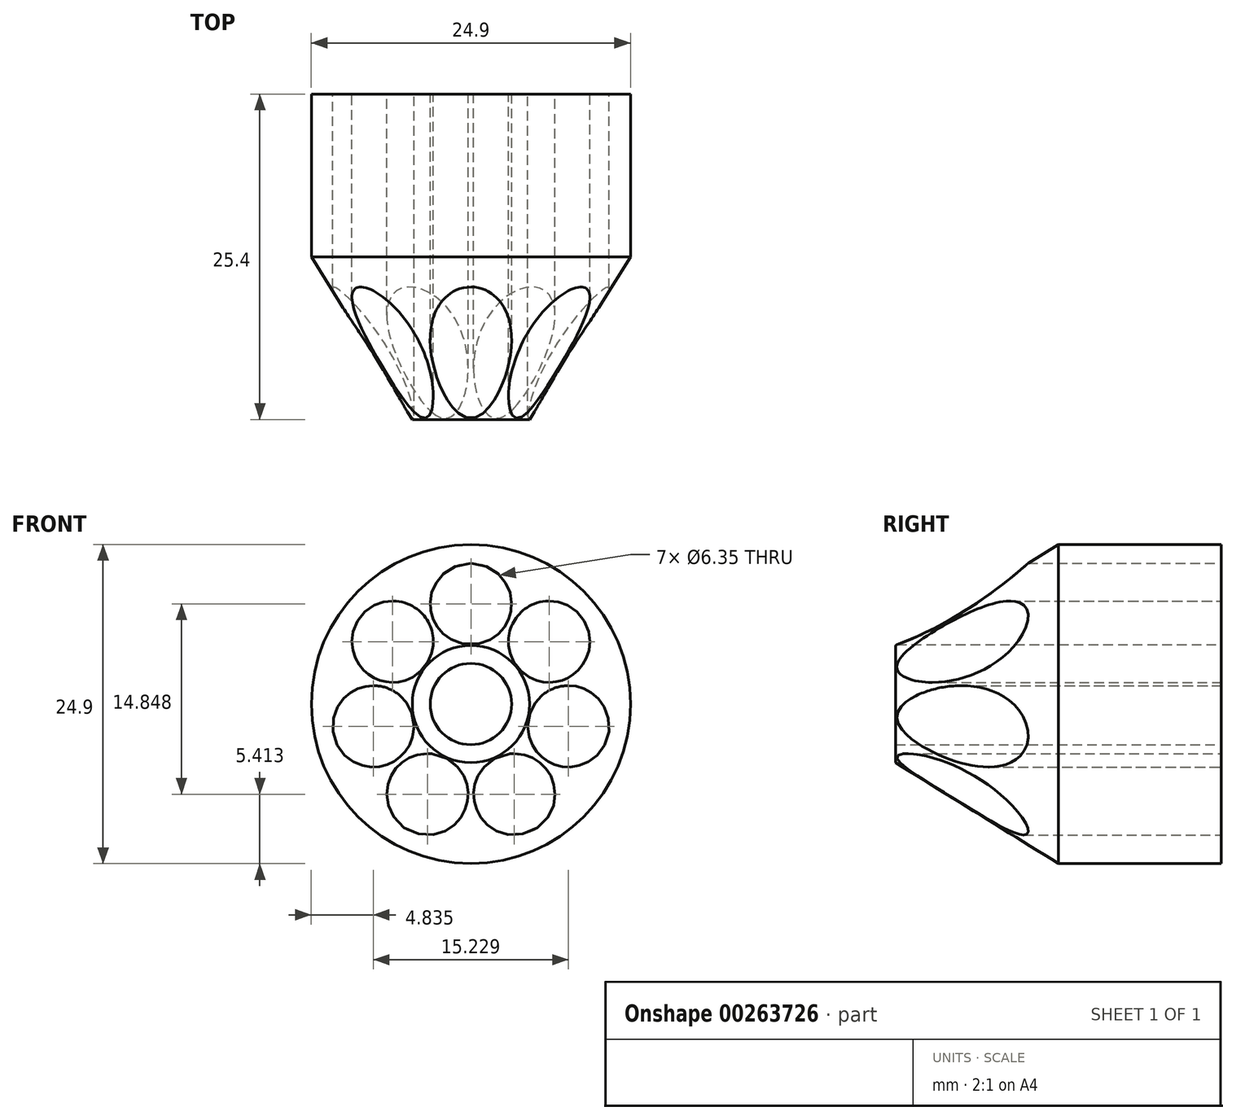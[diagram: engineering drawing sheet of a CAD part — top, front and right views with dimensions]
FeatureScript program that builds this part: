
annotation { "Feature Type Name" : "Feature", "Feature Type Description" : "" }
export const myFeature = defineFeature(function(context is Context, id is Id, definition is map)
    precondition{}
    {
        {
            var Q0;
            Q0=qCreatedBy(makeId("Front.planeOp"),FACE);
            var sketch = newSketch(context, id + "F0", { "sketchPlane" : qUnion([Q0])});
            skCircle(sketch, "E0", {"center": v(0, 0) * mm, "radius": 12.45 * mm});
            skCircle(sketch, "E1", {"center": v(0, 0) * mm, "radius": 3.18 * mm});
            skSolve(sketch);
        }
        {
            var Q0;
            Q0=makeQuery(id+"F0.imprint","IMPRINT",FACE,{"disambiguationData":[TD([[makeQuery(id+"F0.imprint","IMPRINT",EDGE,{"derivedFrom":sQuery(id+"F0.wireOp",EDGE,"E0")}),1.0]])]});
            extrude(context, id + "F1", {"entities" : qUnion([Q0]), "depth" : 25.4 * mm});
        }
        {
            var Q0;
            Q0=makeQuery(id+"F1.opExtrude","CAP_FACE",FACE,{"disambiguationData":[OSD([sQuery(id+"F0.wireOp",EDGE,"E0"),sQuery(id+"F0.wireOp",EDGE,"E1")])],"isStart":true});
            var sketch = newSketch(context, id + "F2", { "sketchPlane" : qUnion([Q0])});
            skLineSegment(sketch, "E2", {"start": v(0, 3.17) * mm, "end": v(0, 12.45) * mm});
            skCircle(sketch, "E3.cCircle", {"center": v(0, 0) * mm, "radius": 7.81 * mm, "construction": true});
            skLineSegment(sketch, "E3.0", {"start": v(0, 7.81) * mm, "end": v(6.1, 4.87) * mm});
            skLineSegment(sketch, "E3.1", {"start": v(6.1, 4.87) * mm, "end": v(7.61, -1.74) * mm});
            skLineSegment(sketch, "E3.2", {"start": v(7.61, -1.74) * mm, "end": v(3.39, -7.04) * mm});
            skLineSegment(sketch, "E3.3", {"start": v(3.39, -7.04) * mm, "end": v(-3.39, -7.04) * mm});
            skLineSegment(sketch, "E3.4", {"start": v(-3.39, -7.04) * mm, "end": v(-7.61, -1.74) * mm});
            skLineSegment(sketch, "E3.5", {"start": v(-7.61, -1.74) * mm, "end": v(-6.1, 4.87) * mm});
            skLineSegment(sketch, "E3.6", {"start": v(-6.1, 4.87) * mm, "end": v(0, 7.81) * mm});
            skPoint(sketch, "E4", {"position": v(0, 7.81) * mm});
            skPoint(sketch, "E5", {"position": v(6.1, 4.87) * mm});
            skPoint(sketch, "E6", {"position": v(7.61, -1.74) * mm});
            skPoint(sketch, "E7", {"position": v(3.39, -7.04) * mm});
            skPoint(sketch, "E8", {"position": v(-3.39, -7.04) * mm});
            skPoint(sketch, "E9", {"position": v(-7.61, -1.74) * mm});
            skPoint(sketch, "E10", {"position": v(-6.1, 4.87) * mm});
            skSolve(sketch);
        }
        {
            var Q0;
            Q0=sQuery(id+"F2.wireOp",VERTEX,"E4");
            var Q1;
            Q1=sQuery(id+"F2.wireOp",VERTEX,"E5");
            var Q2;
            Q2=sQuery(id+"F2.wireOp",VERTEX,"E6");
            var Q3;
            Q3=sQuery(id+"F2.wireOp",VERTEX,"E7");
            var Q4;
            Q4=sQuery(id+"F2.wireOp",VERTEX,"E8");
            var Q5;
            Q5=sQuery(id+"F2.wireOp",VERTEX,"E9");
            var Q6;
            Q6=sQuery(id+"F2.wireOp",VERTEX,"E10");
            var Q7;
            Q7=makeQuery(id+"F1.opExtrude","SWEPT_BODY",BODY,{"disambiguationData":[OSD([sQuery(id+"F0.wireOp",EDGE,"E0"),sQuery(id+"F0.wireOp",EDGE,"E1")])]});
            hole(context, id + "F3", {"style" : HoleStyle.SIMPLE, "endStyle" : HoleEndStyle.THROUGH, "holeDiameter" : 6.35 * mm, "tappedDepth" : 12.7 * mm, "tapClearance" : 3, "locations" : qUnion([Q0, Q1, Q2, Q3, Q4, Q5, Q6]), "scope" : qUnion([Q7])});
        }
        {
            var Q0;
            Q0=makeQuery(id+"F1.opExtrude","CAP_FACE",FACE,{"disambiguationData":[OSD([sQuery(id+"F0.wireOp",EDGE,"E0"),sQuery(id+"F0.wireOp",EDGE,"E1")])],"isStart":false});
            var sketch = newSketch(context, id + "F4", { "sketchPlane" : qUnion([Q0])});
            skCircle(sketch, "E11", {"center": v(0, 0) * mm, "radius": 4.64 * mm});
            skSolve(sketch);
        }
        {
            var Q0;
            Q0=makeQuery(id+"F1.opExtrude","CAP_FACE",FACE,{"disambiguationData":[OSD([sQuery(id+"F0.wireOp",EDGE,"E0"),sQuery(id+"F0.wireOp",EDGE,"E1")])],"isStart":false});
            cPlane(context, id + "F5", {"entities" : qUnion([Q0]), "cplaneType" : CPlaneType.OFFSET, "offset" : 12.7 * mm, "oppositeDirection" : true, "width" : 152.4 * mm, "height" : 152.4 * mm});
        }
        {
            var Q0;
            Q0=makeQuery(id+"F1.opExtrude","CAP_EDGE",EDGE,{"disambiguationData":[OSD([sQuery(id+"F0.wireOp",EDGE,"E0")])],"isStart":false});
            chamfer(context, id + "F6", {"entities" : qUnion([Q0]), "chamferType" : ChamferType.TWO_OFFSETS, "width1" : 7.87 * mm, "oppositeDirection" : false, "width2" : 12.7 * mm, "tangentPropagation" : true});
        }
    });
